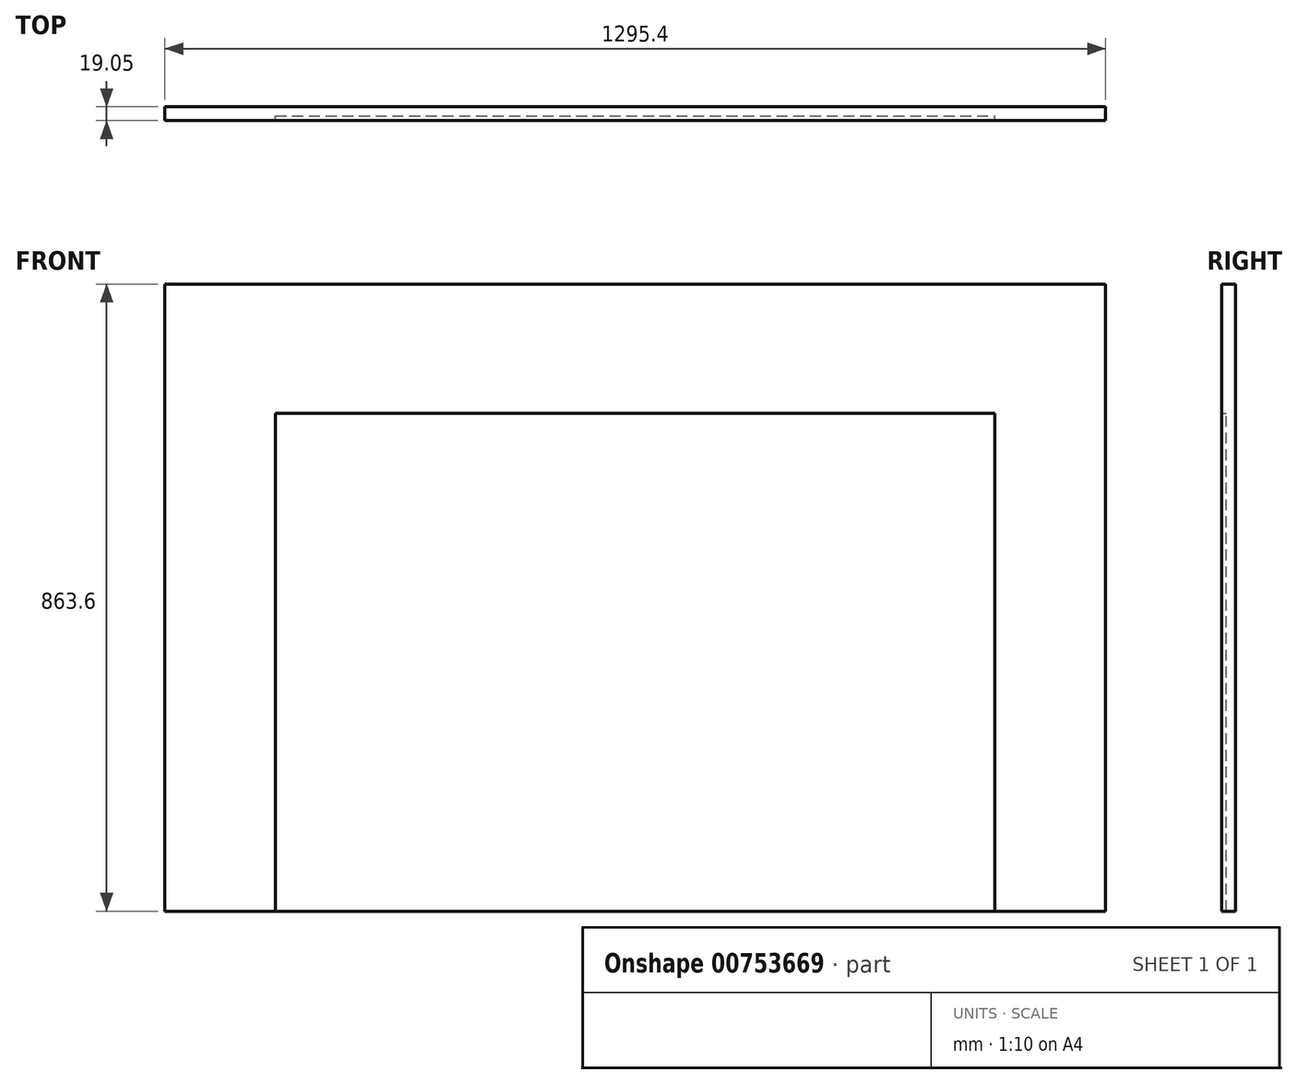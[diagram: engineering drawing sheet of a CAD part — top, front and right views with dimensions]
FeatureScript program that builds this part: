
annotation { "Feature Type Name" : "Feature", "Feature Type Description" : "" }
export const myFeature = defineFeature(function(context is Context, id is Id, definition is map)
    precondition{}
    {
        {
            var Q0;
            Q0=qCreatedBy(makeId("Front.planeOp"),FACE);
            var sketch = newSketch(context, id + "F0", { "sketchPlane" : qUnion([Q0])});
            skLineSegment(sketch, "E0.bottom", {"start": v(0, 0) * mm, "end": v(990.6, 0) * mm});
            skLineSegment(sketch, "E0.top", {"start": v(0, 685.8) * mm, "end": v(990.6, 685.8) * mm});
            skLineSegment(sketch, "E0.left", {"start": v(0, 0) * mm, "end": v(0, 685.8) * mm});
            skLineSegment(sketch, "E0.right", {"start": v(990.6, 0) * mm, "end": v(990.6, 685.8) * mm});
            skSolve(sketch);
        }
        {
            var Q0;
            Q0 = qSketchRegion(id + "F0", true);
            extrude(context, id + "F1", {"entities" : qUnion([Q0]), "depth" : 12.7 * mm, "offsetDistance" : 25.4 * mm});
        }
        {
            var Q0;
            Q0=qCreatedBy(makeId("Front.planeOp"),FACE);
            var sketch = newSketch(context, id + "F2", { "sketchPlane" : qUnion([Q0])});
            skLineSegment(sketch, "E1.bottom", {"start": v(0, 0) * mm, "end": v(-152.4, 0) * mm});
            skLineSegment(sketch, "E1.top", {"start": v(0, 863.6) * mm, "end": v(-152.4, 863.6) * mm});
            skLineSegment(sketch, "E1.left", {"start": v(0, 0) * mm, "end": v(0, 685.8) * mm});
            skLineSegment(sketch, "E1.right", {"start": v(-152.4, 0) * mm, "end": v(-152.4, 863.6) * mm});
            skLineSegment(sketch, "E2.bottom", {"start": v(0, 863.6) * mm, "end": v(990.6, 863.6) * mm});
            skLineSegment(sketch, "E2.top", {"start": v(0, 685.8) * mm, "end": v(990.6, 685.8) * mm});
            skLineSegment(sketch, "E3.bottom", {"start": v(990.6, 0) * mm, "end": v(1143, 0) * mm});
            skLineSegment(sketch, "E3.top", {"start": v(990.6, 863.6) * mm, "end": v(1143, 863.6) * mm});
            skLineSegment(sketch, "E3.left", {"start": v(990.6, 0) * mm, "end": v(990.6, 685.8) * mm});
            skLineSegment(sketch, "E3.right", {"start": v(1143, 0) * mm, "end": v(1143, 863.6) * mm});
            skSolve(sketch);
        }
        {
            var Q0;
            Q0=makeQuery(id+"F2.imprint","IMPRINT",FACE,{"disambiguationData":[TD([[makeQuery(id+"F2.imprint","IMPRINT",EDGE,{"derivedFrom":sQuery(id+"F2.wireOp",EDGE,"E1.bottom")}),-1.0]])]});
            extrude(context, id + "F3", {"entities" : qUnion([Q0]), "operationType" : NewBodyOperationType.ADD, "depth" : 19.05 * mm, "offsetDistance" : 25.4 * mm});
        }
    });
